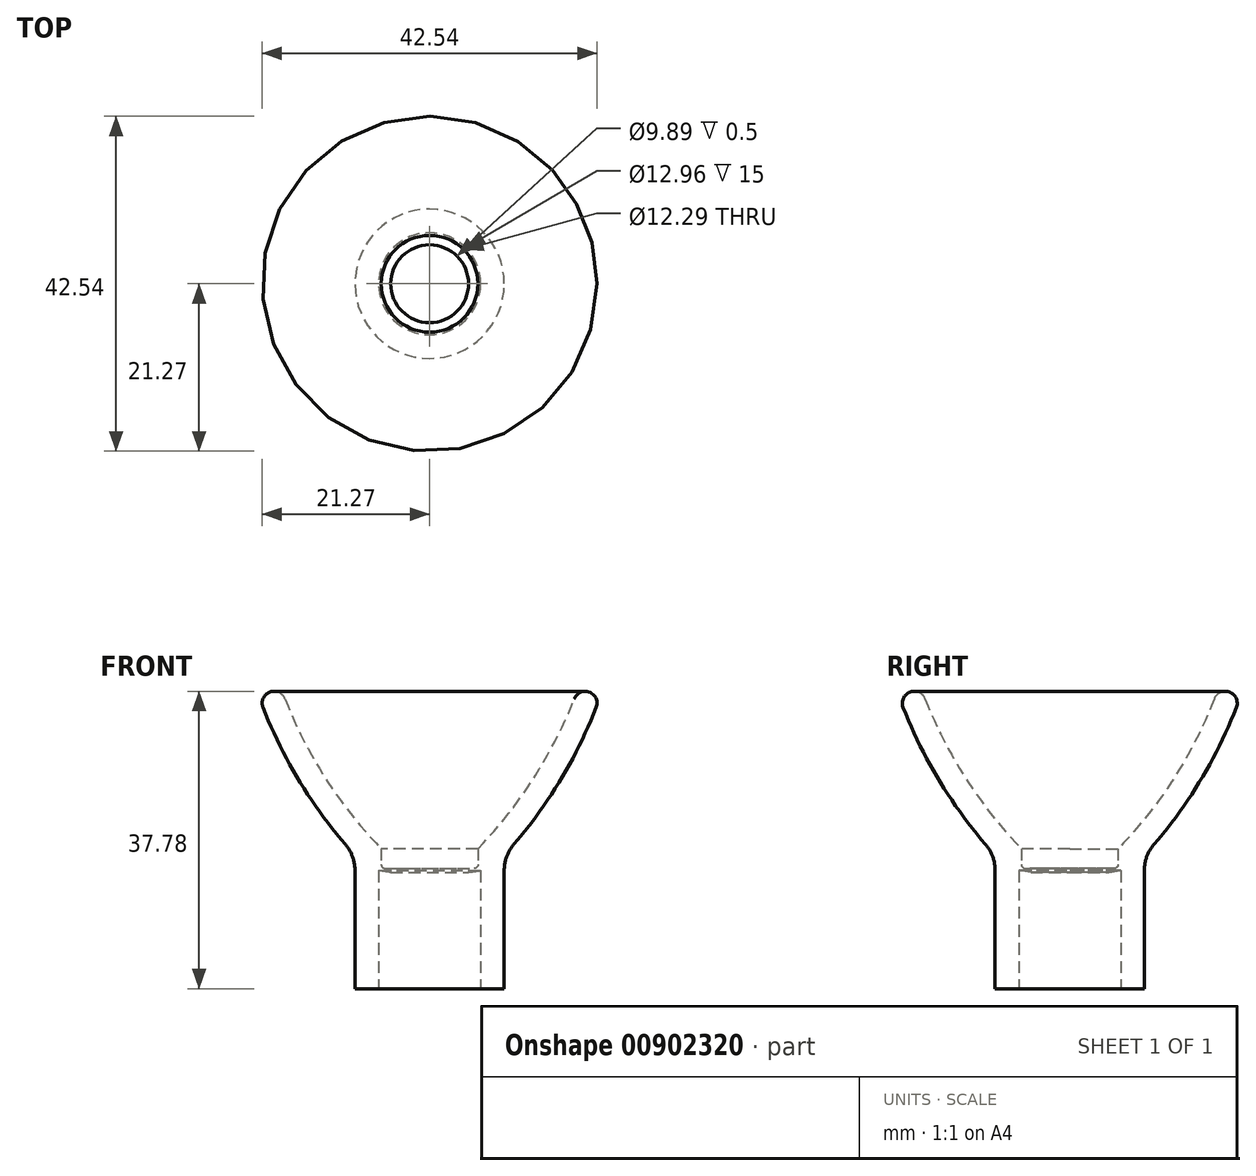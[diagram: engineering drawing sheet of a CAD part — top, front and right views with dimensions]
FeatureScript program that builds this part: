
annotation { "Feature Type Name" : "Feature", "Feature Type Description" : "" }
export const myFeature = defineFeature(function(context is Context, id is Id, definition is map)
    precondition{}
    {
        {
            var Q0;
            Q0=qCreatedBy(makeId("Front.planeOp"),FACE);
            var sketch = newSketch(context, id + "F0", { "sketchPlane" : qUnion([Q0])});
            skLineSegment(sketch, "E0", {"start": v(0, 0) * mm, "end": v(6.48, 0) * mm, "construction": true});
            skLineSegment(sketch, "E1", {"start": v(0, 0) * mm, "end": v(0, 36.8) * mm, "construction": true});
            skLineSegment(sketch, "E2", {"start": v(6.48, 0) * mm, "end": v(6.48, 15) * mm});
            skLineSegment(sketch, "E3", {"start": v(6.48, 15) * mm, "end": v(4.95, 14.78) * mm});
            skLineSegment(sketch, "E4", {"start": v(4.95, 14.78) * mm, "end": v(4.95, 15.28) * mm});
            skLineSegment(sketch, "E5", {"start": v(4.95, 15.28) * mm, "end": v(5.65, 15.28) * mm});
            skLineSegment(sketch, "E6", {"start": v(6.15, 15.78) * mm, "end": v(6.15, 17.47) * mm});
            skPoint(sketch, "E7.visualSharp", {"position": v(6.15, 15.28) * mm});
            skArc(sketch, "E7.filletArc", {"start": v(5.65, 15.28) * mm, "mid": v(6, 15.42) * mm, "end": v(6.15, 15.78) * mm});
            skPoint(sketch, "E8.visualSharp", {"position": v(6.15, 17.78) * mm});
            skLineSegment(sketch, "E9", {"start": v(6.15, 17.47) * mm, "end": v(6.15, 17.78) * mm});
            skArc(sketch, "E10", {"start": v(6.15, 17.78) * mm, "mid": v(15.38, 30.37) * mm, "end": v(20.9, 44.99) * mm});
            skArc(sketch, "E11.0", {"start": v(9.48, 16.94) * mm, "mid": v(18.47, 29.8) * mm, "end": v(23.87, 44.54) * mm});
            skLineSegment(sketch, "E11.1", {"start": v(9.48, 0) * mm, "end": v(9.48, 16.94) * mm});
            skLineSegment(sketch, "E12", {"start": v(23.87, 44.54) * mm, "end": v(23.87, 44.65) * mm});
            skLineSegment(sketch, "E13", {"start": v(22.37, 46.15) * mm, "end": v(22.35, 46.15) * mm});
            skPoint(sketch, "E14.visualSharp", {"position": v(21.15, 46.15) * mm});
            skArc(sketch, "E14.filletArc", {"start": v(22.35, 46.15) * mm, "mid": v(21.42, 45.82) * mm, "end": v(20.9, 44.99) * mm});
            skPoint(sketch, "E15.visualSharp", {"position": v(23.87, 46.15) * mm});
            skArc(sketch, "E15.filletArc", {"start": v(23.87, 44.65) * mm, "mid": v(23.43, 45.71) * mm, "end": v(22.37, 46.15) * mm});
            skLineSegment(sketch, "E16", {"start": v(9.48, 0) * mm, "end": v(6.48, 0) * mm});
            skSolve(sketch);
        }
        {
            var Q0;
            Q0=makeQuery(id+"F0.imprint","IMPRINT",FACE,{"disambiguationData":[TD([[makeQuery(id+"F0.imprint","IMPRINT",EDGE,{"derivedFrom":sQuery(id+"F0.wireOp",EDGE,"E2")}),-1.0]])]});
            var Q1;
            Q1=sQuery(id+"F0.wireOp",EDGE,"E1");
            revolve(context, id + "F1", {"surfaceOperationType" : NewSurfaceOperationType.NEW, "entities" : qUnion([Q0]), "axis" : qUnion([Q1]), "revolveType" : RevolveType.FULL});
        }
        {
            var Q0;
            Q0=qCreatedBy(makeId("Front.planeOp"),FACE);
            var sketch = newSketch(context, id + "F2", { "sketchPlane" : qUnion([Q0])});
            skLineSegment(sketch, "E17", {"start": v(-31.6, 37.78) * mm, "end": v(39.34, 37.78) * mm});
            skLineSegment(sketch, "E18", {"start": v(39.34, 37.78) * mm, "end": v(39.34, 48.98) * mm});
            skLineSegment(sketch, "E19", {"start": v(39.34, 48.98) * mm, "end": v(-31.6, 48.98) * mm});
            skLineSegment(sketch, "E20", {"start": v(-31.6, 48.98) * mm, "end": v(-31.6, 37.78) * mm});
            skSolve(sketch);
        }
        {
            var Q0;
            Q0=makeQuery(id+"F2.imprint","IMPRINT",FACE,{"disambiguationData":[TD([[makeQuery(id+"F2.imprint","IMPRINT",EDGE,{"derivedFrom":sQuery(id+"F2.wireOp",EDGE,"E17")}),1.0]])]});
            extrude(context, id + "F3", {"entities" : qUnion([Q0]), "operationType" : NewBodyOperationType.REMOVE, "endBound" : BoundingType.SYMMETRIC, "depth" : 50 * mm, "offsetDistance" : 25 * mm});
        }
        {
            var Q0;
            Q0=makeQuery(id+"F3.boolean.opBoolean","INTERSECT",EDGE,{"derivedFrom":[makeQuery(id+"F1.opRevolve","SWEPT_FACE",FACE,{"disambiguationData":[OSD([sQuery(id+"F0.wireOp",EDGE,"E11.0")])]}),makeQuery(id+"F3.opExtrude","SWEPT_FACE",FACE,{"disambiguationData":[OSD([sQuery(id+"F2.wireOp",EDGE,"E17")])]})]});
            var Q1;
            Q1=makeQuery(id+"F3.boolean.opBoolean","INTERSECT",EDGE,{"derivedFrom":[makeQuery(id+"F1.opRevolve","SWEPT_FACE",FACE,{"disambiguationData":[OSD([sQuery(id+"F0.wireOp",EDGE,"E10")])]}),makeQuery(id+"F3.opExtrude","SWEPT_FACE",FACE,{"disambiguationData":[OSD([sQuery(id+"F2.wireOp",EDGE,"E17")])]})]});
            fillet(context, id + "F4", {"entities" : qUnion([Q0, Q1]), "radius" : 1.5 * mm, "tangentPropagation" : true, "allowEdgeOverflow" : false});
        }
        {
            var Q0;
            Q0=makeQuery(id+"F1.opRevolve","SWEPT_EDGE",EDGE,{"disambiguationData":[OSD([sQuery(id+"F0.wireOp",EDGE,"E11.0"),sQuery(id+"F0.wireOp",EDGE,"E11.1")])]});
            fillet(context, id + "F5", {"entities" : qUnion([Q0]), "radius" : 5 * mm, "tangentPropagation" : true, "allowEdgeOverflow" : false});
        }
    });
